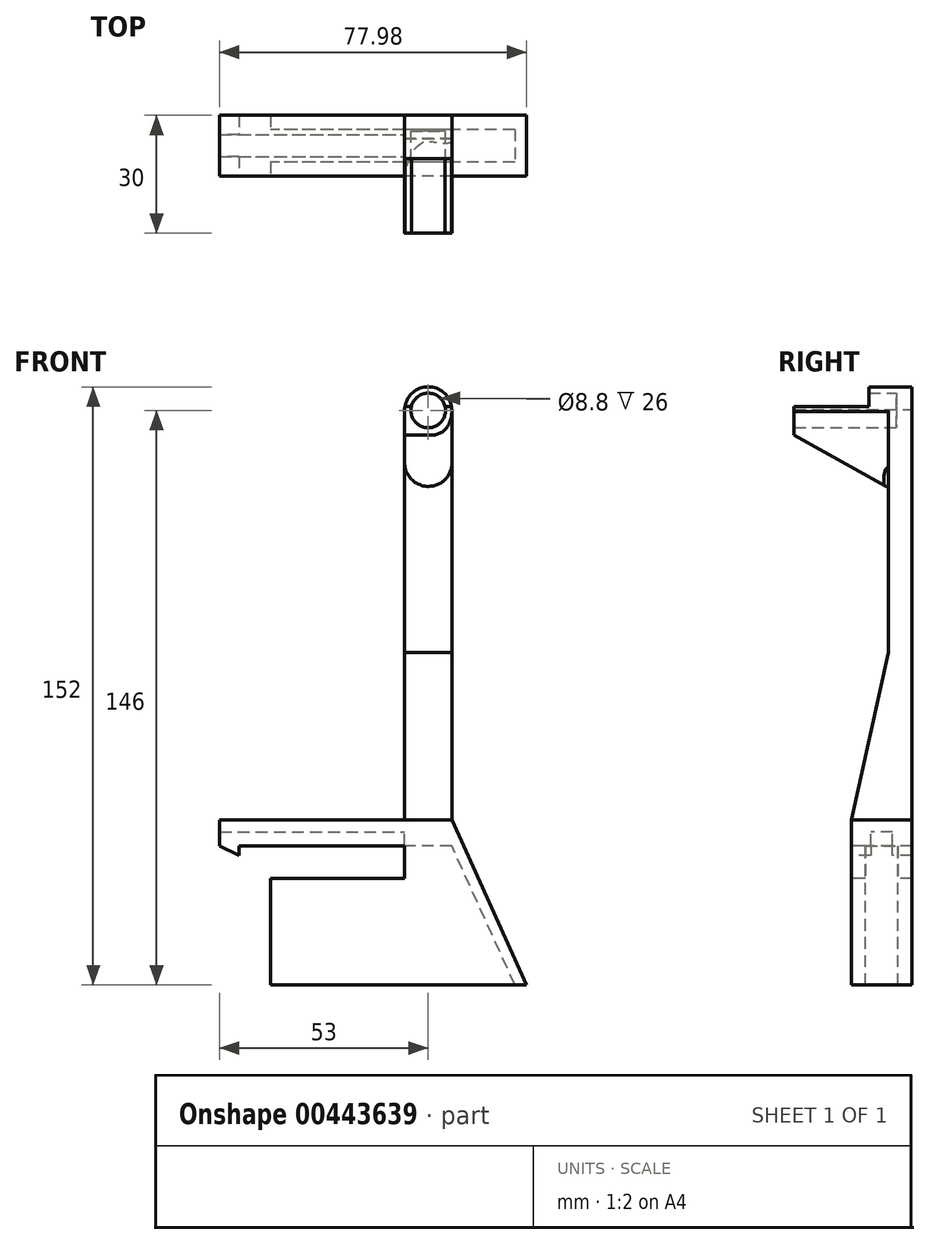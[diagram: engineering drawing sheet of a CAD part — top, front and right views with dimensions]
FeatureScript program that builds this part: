
annotation { "Feature Type Name" : "Feature", "Feature Type Description" : "" }
export const myFeature = defineFeature(function(context is Context, id is Id, definition is map)
    precondition{}
    {
        {
            var Q0;
            Q0=qCreatedBy(makeId("Front.planeOp"),FACE);
            var sketch = newSketch(context, id + "F0", { "sketchPlane" : qUnion([Q0])});
            skLineSegment(sketch, "E0.bottom", {"start": v(-6, 50) * mm, "end": v(6, 50) * mm});
            skLineSegment(sketch, "E0.top", {"start": v(-6, -50) * mm, "end": v(6, -50) * mm});
            skLineSegment(sketch, "E0.left", {"start": v(-6, 50) * mm, "end": v(-6, -50) * mm});
            skLineSegment(sketch, "E0.right", {"start": v(6, 50) * mm, "end": v(6, -50) * mm});
            skPoint(sketch, "E0.middle", {"position": v(0, 0) * mm});
            skLineSegment(sketch, "E1", {"start": v(0, 0) * mm, "end": v(0, 97.6) * mm, "construction": true});
            skCircle(sketch, "E2", {"center": v(0, 56) * mm, "radius": 6 * mm});
            skCircle(sketch, "E3", {"center": v(0, 56) * mm, "radius": 4.4 * mm});
            skLineSegment(sketch, "E4", {"start": v(-6, 56.27) * mm, "end": v(-6, 50) * mm});
            skLineSegment(sketch, "E5", {"start": v(6, 50) * mm, "end": v(6, 56) * mm});
            skSolve(sketch);
        }
        {
            var Q0;
            {var subQ0=sQuery(id+"F0.wireOp",EDGE,"E0.bottom");Q0=makeQuery(id+"F0.imprint","IMPRINT",FACE,{"disambiguationData":[TD([[makeQuery(id+"F0.imprint","IMPRINT",EDGE,{"derivedFrom":subQ0}),1.0]])]});}
            var Q1;
            Q1=makeQuery(id+"F0.imprint","IMPRINT",FACE,{"disambiguationData":[TD([[makeQuery(id+"F0.imprint","IMPRINT",EDGE,{"derivedFrom":sQuery(id+"F0.wireOp",EDGE,"E3")}),-1.0]])]});
            var Q2;
            Q2=makeQuery(id+"F0.imprint","IMPRINT",FACE,{"disambiguationData":[TD([[makeQuery(id+"F0.imprint","IMPRINT",EDGE,{"derivedFrom":sQuery(id+"F0.wireOp",EDGE,"E0.bottom")}),-1.0]])]});
            var Q3;
            Q3=makeQuery(id+"F0.imprint","IMPRINT",FACE,{"disambiguationData":[TD([[makeQuery(id+"F0.imprint","IMPRINT",EDGE,{"derivedFrom":sQuery(id+"F0.wireOp",EDGE,"E3")}),1.0]])]});
            extrude(context, id + "F1", {"entities" : qUnion([Q0, Q1, Q2, Q3]), "depth" : 6 * mm});
        }
        {
            var Q0;
            Q0=makeQuery(id+"F0.imprint","IMPRINT",FACE,{"disambiguationData":[TD([[makeQuery(id+"F0.imprint","IMPRINT",EDGE,{"derivedFrom":sQuery(id+"F0.wireOp",EDGE,"E3")}),-1.0]])]});
            extrude(context, id + "F2", {"entities" : qUnion([Q0]), "operationType" : NewBodyOperationType.ADD, "depth" : 30 * mm});
        }
        {
            var Q0;
            Q0=makeQuery(id+"F1.opExtrude","SWEPT_FACE",FACE,{"disambiguationData":[OSD([sQuery(id+"F0.wireOp",EDGE,"E0.left")])]});
            var sketch = newSketch(context, id + "F3", { "sketchPlane" : qUnion([Q0])});
            skLineSegment(sketch, "E6.bottom", {"start": v(0, -50) * mm, "end": v(15.47, -50) * mm});
            skLineSegment(sketch, "E6.top", {"start": v(0, -90) * mm, "end": v(15.47, -90) * mm});
            skLineSegment(sketch, "E6.left", {"start": v(0, -50) * mm, "end": v(0, -90) * mm});
            skLineSegment(sketch, "E6.right", {"start": v(15.47, -50) * mm, "end": v(15.47, -90) * mm});
            skPoint(sketch, "E7", {"position": v(0, -50) * mm});
            skLineSegment(sketch, "E8.bottom", {"start": v(3.61, -54.6) * mm, "end": v(11.86, -54.6) * mm});
            skLineSegment(sketch, "E8.top", {"start": v(3.61, -90) * mm, "end": v(11.86, -90) * mm});
            skLineSegment(sketch, "E8.left", {"start": v(3.61, -54.6) * mm, "end": v(3.61, -90) * mm});
            skLineSegment(sketch, "E8.right", {"start": v(11.86, -54.6) * mm, "end": v(11.86, -90) * mm});
            skPoint(sketch, "E9", {"position": v(7.74, -54.6) * mm});
            skPoint(sketch, "E10", {"position": v(7.74, -50) * mm});
            skLineSegment(sketch, "E11", {"start": v(15.47, -50) * mm, "end": v(15.47, -48) * mm});
            skLineSegment(sketch, "E12", {"start": v(15.47, -48) * mm, "end": v(6, -5.52) * mm});
            skSolve(sketch);
        }
        {
            var Q0;
            {var subQ4=sQuery(id+"F3.wireOp",EDGE,"E6.left");Q0=makeQuery(id+"F3.imprint","IMPRINT",FACE,{"disambiguationData":[TD([[makeQuery(id+"F3.imprint","IMPRINT",EDGE,{"derivedFrom":subQ4}),1.0]])]});}
            var Q1;
            {var subQ3=sQuery(id+"F3.wireOp",EDGE,"npjAtSIb-rjZG-cwZH-Mb7X-xIMRF1PIqRGn");Q1=makeQuery(id+"F3.imprint","IMPRINT",FACE,{"disambiguationData":[TD([[makeQuery(id+"F3.imprint","IMPRINT",EDGE,{"derivedFrom":subQ3}),1.0]])]});}
            var Q2;
            {var subQ3=sQuery(id+"F3.wireOp",EDGE,"E11");Q2=makeQuery(id+"F3.imprint","IMPRINT",FACE,{"disambiguationData":[TD([[makeQuery(id+"F3.imprint","IMPRINT",EDGE,{"derivedFrom":subQ3}),1.0]])]});}
            var Q3;
            Q3=makeQuery(id+"F1.opExtrude","SWEPT_FACE",FACE,{"disambiguationData":[OSD([sQuery(id+"F0.wireOp",EDGE,"E0.right"),sQuery(id+"F0.wireOp",EDGE,"E5")])]});
            extrude(context, id + "F4", {"entities" : qUnion([Q0, Q1, Q2]), "operationType" : NewBodyOperationType.ADD, "endBound" : BoundingType.UP_TO_SURFACE, "oppositeDirection" : true, "endBoundEntityFace" : qUnion([Q3]), "depth" : 25 * mm});
        }
        {
            var Q0;
            {var subQ0=sQuery(id+"F0.wireOp",EDGE,"E0.left");Q0=makeQuery(id+"F4.boolean.opBoolean","MERGE",FACE,{"derivedFrom":[makeQuery(id+"F1.opExtrude","SWEPT_FACE",FACE,{"disambiguationData":[OSD([subQ0])]}),makeQuery(id+"F4.opExtrude","CAP_FACE",FACE,{"disambiguationData":[OSD([subQ0,sQuery(id+"F3.wireOp",EDGE,"E6.bottom"),sQuery(id+"F3.wireOp",EDGE,"E6.top"),sQuery(id+"F3.wireOp",EDGE,"E6.left"),sQuery(id+"F3.wireOp",EDGE,"E6.right"),sQuery(id+"F3.wireOp",EDGE,"E8.bottom"),sQuery(id+"F3.wireOp",EDGE,"E8.left"),sQuery(id+"F3.wireOp",EDGE,"E8.right"),sQuery(id+"F3.wireOp",EDGE,"E11"),sQuery(id+"F3.wireOp",EDGE,"E12")])],"isStart":true})]});}
            var sketch = newSketch(context, id + "F5", { "sketchPlane" : qUnion([Q0])});
            skLineSegment(sketch, "E13.bottom", {"start": v(0, -48) * mm, "end": v(15.47, -48) * mm});
            skLineSegment(sketch, "E13.top", {"start": v(0, -54.6) * mm, "end": v(15.47, -54.6) * mm});
            skLineSegment(sketch, "E13.left", {"start": v(0, -48) * mm, "end": v(0, -54.6) * mm});
            skLineSegment(sketch, "E13.right", {"start": v(15.47, -48) * mm, "end": v(15.47, -54.6) * mm});
            skLineSegment(sketch, "E14.bottom", {"start": v(4.99, -54.6) * mm, "end": v(10.49, -54.6) * mm});
            skLineSegment(sketch, "E14.top", {"start": v(4.99, -51.1) * mm, "end": v(10.49, -51.1) * mm});
            skLineSegment(sketch, "E14.left", {"start": v(4.99, -54.6) * mm, "end": v(4.99, -51.1) * mm});
            skLineSegment(sketch, "E14.right", {"start": v(10.49, -54.6) * mm, "end": v(10.49, -51.1) * mm});
            skPoint(sketch, "E15", {"position": v(7.74, -51.1) * mm});
            skPoint(sketch, "E16", {"position": v(7.74, -54.6) * mm});
            skSolve(sketch);
        }
        {
            var Q0;
            Q0=makeQuery(id+"F5.imprint","IMPRINT",FACE,{"disambiguationData":[TD([[makeQuery(id+"F5.imprint","IMPRINT",EDGE,{"derivedFrom":sQuery(id+"F5.wireOp",EDGE,"E13.bottom")}),-1.0]])]});
            extrude(context, id + "F6", {"entities" : qUnion([Q0]), "operationType" : NewBodyOperationType.ADD, "depth" : 47 * mm});
        }
        {
            var Q0;
            Q0=makeQuery(id+"F6.boolean.opBoolean","MERGE",FACE,{"derivedFrom":[makeQuery(id+"F4.opExtrude","SWEPT_FACE",FACE,{"disambiguationData":[OSD([sQuery(id+"F3.wireOp",EDGE,"E6.right"),sQuery(id+"F3.wireOp",EDGE,"E11")])]}),makeQuery(id+"F6.opExtrude","SWEPT_FACE",FACE,{"disambiguationData":[OSD([sQuery(id+"F5.wireOp",EDGE,"E13.right")])]})]});
            var sketch = newSketch(context, id + "F7", { "sketchPlane" : qUnion([Q0])});
            skLineSegment(sketch, "E17", {"start": v(-53, -54.6) * mm, "end": v(-48, -54.6) * mm});
            skLineSegment(sketch, "E18", {"start": v(-48, -54.6) * mm, "end": v(-48, -57.1) * mm});
            skLineSegment(sketch, "E19", {"start": v(-48, -57.1) * mm, "end": v(-53, -54.6) * mm});
            skSolve(sketch);
        }
        {
            var Q0;
            Q0=makeQuery(id+"F7.imprint","IMPRINT",FACE,{"disambiguationData":[TD([[makeQuery(id+"F7.imprint","IMPRINT",EDGE,{"derivedFrom":sQuery(id+"F7.wireOp",EDGE,"E17")}),-1.0]])]});
            var Q1;
            Q1=makeQuery(id+"F6.opExtrude","CAP_VERTEX",VERTEX,{"disambiguationData":[OSD([sQuery(id+"F5.wireOp",EDGE,"E13.top"),sQuery(id+"F5.wireOp",EDGE,"E14.bottom"),sQuery(id+"F5.wireOp",EDGE,"E14.right")])],"isStart":false});
            extrude(context, id + "F8", {"entities" : qUnion([Q0]), "operationType" : NewBodyOperationType.ADD, "endBound" : BoundingType.UP_TO_VERTEX, "oppositeDirection" : true, "endBoundEntityVertex" : qUnion([Q1]), "depth" : 25 * mm});
        }
        {
            var Q0;
            Q0=makeQuery(id+"F7.imprint","IMPRINT",FACE,{"disambiguationData":[TD([[makeQuery(id+"F7.imprint","IMPRINT",EDGE,{"derivedFrom":sQuery(id+"F7.wireOp",EDGE,"E17")}),-1.0]])]});
            var Q1;
            Q1=makeQuery(id+"F6.opExtrude","CAP_VERTEX",VERTEX,{"disambiguationData":[OSD([sQuery(id+"F0.wireOp",EDGE,"E0.left"),sQuery(id+"F3.wireOp",EDGE,"E6.left"),sQuery(id+"F5.wireOp",EDGE,"E13.top"),sQuery(id+"F5.wireOp",EDGE,"E13.left")])],"isStart":false});
            var Q2;
            Q2=makeQuery(id+"F6.opExtrude","CAP_VERTEX",VERTEX,{"disambiguationData":[OSD([sQuery(id+"F5.wireOp",EDGE,"E13.top"),sQuery(id+"F5.wireOp",EDGE,"E14.bottom"),sQuery(id+"F5.wireOp",EDGE,"E14.left")])],"isStart":false});
            extrude(context, id + "F9", {"entities" : qUnion([Q0]), "operationType" : NewBodyOperationType.ADD, "endBound" : BoundingType.UP_TO_VERTEX, "oppositeDirection" : true, "endBoundEntityVertex" : qUnion([Q1]), "depth" : 25 * mm, "hasSecondDirection" : true, "secondDirectionBound" : SecondDirectionBoundingType.UP_TO_VERTEX, "secondDirectionOppositeDirection" : true, "secondDirectionBoundEntityVertex" : qUnion([Q2]), "secondDirectionDepth" : 25 * mm});
        }
        {
            var Q0;
            Q0=makeQuery(id+"F8.boolean.opBoolean","MERGE",FACE,{"derivedFrom":[makeQuery(id+"F6.boolean.opBoolean","MERGE",FACE,{"derivedFrom":[makeQuery(id+"F4.opExtrude","SWEPT_FACE",FACE,{"disambiguationData":[OSD([sQuery(id+"F3.wireOp",EDGE,"E6.right"),sQuery(id+"F3.wireOp",EDGE,"E11")])]}),makeQuery(id+"F6.opExtrude","SWEPT_FACE",FACE,{"disambiguationData":[OSD([sQuery(id+"F5.wireOp",EDGE,"E13.right")])]})]}),makeQuery(id+"F8.opExtrude","CAP_FACE",FACE,{"disambiguationData":[OSD([sQuery(id+"F7.wireOp",EDGE,"E17"),sQuery(id+"F7.wireOp",EDGE,"E18"),sQuery(id+"F7.wireOp",EDGE,"E19")])],"isStart":true})]});
            var sketch = newSketch(context, id + "F10", { "sketchPlane" : qUnion([Q0])});
            skLineSegment(sketch, "E20.bottom", {"start": v(-6, -90) * mm, "end": v(-40, -90) * mm});
            skLineSegment(sketch, "E20.top", {"start": v(-6, -62.85) * mm, "end": v(-40, -62.85) * mm});
            skLineSegment(sketch, "E20.left", {"start": v(-6, -90) * mm, "end": v(-6, -62.85) * mm});
            skLineSegment(sketch, "E20.right", {"start": v(-40, -90) * mm, "end": v(-40, -62.85) * mm});
            skSolve(sketch);
        }
        {
            var Q0;
            Q0=makeQuery(id+"F10.imprint","IMPRINT",FACE,{"disambiguationData":[TD([[makeQuery(id+"F10.imprint","IMPRINT",EDGE,{"derivedFrom":sQuery(id+"F10.wireOp",EDGE,"E20.bottom")}),-1.0]])]});
            var Q1;
            Q1=makeQuery(id+"F4.opExtrude","SWEPT_FACE",FACE,{"disambiguationData":[OSD([sQuery(id+"F3.wireOp",EDGE,"E8.right")])]});
            extrude(context, id + "F11", {"entities" : qUnion([Q0]), "operationType" : NewBodyOperationType.ADD, "endBound" : BoundingType.UP_TO_SURFACE, "oppositeDirection" : true, "endBoundEntityFace" : qUnion([Q1]), "depth" : 25 * mm});
        }
        {
            var Q0;
            Q0=makeQuery(id+"F10.imprint","IMPRINT",FACE,{"disambiguationData":[TD([[makeQuery(id+"F10.imprint","IMPRINT",EDGE,{"derivedFrom":sQuery(id+"F10.wireOp",EDGE,"E20.bottom")}),-1.0]])]});
            var Q1;
            Q1=makeQuery(id+"F9.boolean.opBoolean","MERGE",FACE,{"derivedFrom":[makeQuery(id+"F6.boolean.opBoolean","MERGE",FACE,{"derivedFrom":[makeQuery(id+"F4.boolean.opBoolean","MERGE",FACE,{"derivedFrom":[makeQuery(id+"F1.opExtrude","CAP_FACE",FACE,{"disambiguationData":[OSD([sQuery(id+"F0.wireOp",EDGE,"E0.top"),sQuery(id+"F0.wireOp",EDGE,"E0.left"),sQuery(id+"F0.wireOp",EDGE,"E0.right"),sQuery(id+"F0.wireOp",EDGE,"E2"),sQuery(id+"F0.wireOp",EDGE,"E4"),sQuery(id+"F0.wireOp",EDGE,"E5")])],"isStart":true}),makeQuery(id+"F4.opExtrude","SWEPT_FACE",FACE,{"disambiguationData":[OSD([sQuery(id+"F3.wireOp",EDGE,"E6.left")])]})]}),makeQuery(id+"F6.opExtrude","SWEPT_FACE",FACE,{"disambiguationData":[OSD([sQuery(id+"F5.wireOp",EDGE,"E13.left")])]})]}),makeQuery(id+"F9.opExtrude","CAP_FACE",FACE,{"disambiguationData":[OSD([dummyQuery(id+"F9.vertexPlane.planeOp",FACE)])],"isStart":false})]});
            var Q2;
            Q2=makeQuery(id+"F4.opExtrude","SWEPT_FACE",FACE,{"disambiguationData":[OSD([sQuery(id+"F3.wireOp",EDGE,"E8.left")])]});
            extrude(context, id + "F12", {"entities" : qUnion([Q0]), "operationType" : NewBodyOperationType.ADD, "endBound" : BoundingType.UP_TO_SURFACE, "oppositeDirection" : true, "endBoundEntityFace" : qUnion([Q1]), "depth" : 25 * mm, "hasSecondDirection" : true, "secondDirectionBound" : SecondDirectionBoundingType.UP_TO_SURFACE, "secondDirectionOppositeDirection" : true, "secondDirectionBoundEntityFace" : qUnion([Q2]), "secondDirectionDepth" : 25 * mm});
        }
        {
            var Q0;
            Q0=makeQuery(id+"F11.boolean.opBoolean","MERGE",FACE,{"derivedFrom":[makeQuery(id+"F8.boolean.opBoolean","MERGE",FACE,{"derivedFrom":[makeQuery(id+"F6.boolean.opBoolean","MERGE",FACE,{"derivedFrom":[makeQuery(id+"F4.opExtrude","SWEPT_FACE",FACE,{"disambiguationData":[OSD([sQuery(id+"F3.wireOp",EDGE,"E6.right"),sQuery(id+"F3.wireOp",EDGE,"E11")])]}),makeQuery(id+"F6.opExtrude","SWEPT_FACE",FACE,{"disambiguationData":[OSD([sQuery(id+"F5.wireOp",EDGE,"E13.right")])]})]}),makeQuery(id+"F8.opExtrude","CAP_FACE",FACE,{"disambiguationData":[OSD([sQuery(id+"F7.wireOp",EDGE,"E17"),sQuery(id+"F7.wireOp",EDGE,"E18"),sQuery(id+"F7.wireOp",EDGE,"E19")])],"isStart":true})]}),makeQuery(id+"F11.opExtrude","CAP_FACE",FACE,{"disambiguationData":[OSD([sQuery(id+"F10.wireOp",EDGE,"E20.bottom"),sQuery(id+"F10.wireOp",EDGE,"E20.top"),sQuery(id+"F10.wireOp",EDGE,"E20.left"),sQuery(id+"F10.wireOp",EDGE,"E20.right")])],"isStart":true})]});
            var sketch = newSketch(context, id + "F13", { "sketchPlane" : qUnion([Q0])});
            skLineSegment(sketch, "E21", {"start": v(6, -90) * mm, "end": v(22, -90) * mm});
            skLineSegment(sketch, "E22", {"start": v(22, -90) * mm, "end": v(6, -54.6) * mm});
            skLineSegment(sketch, "E23", {"start": v(6, -54.6) * mm, "end": v(6, -90) * mm});
            skPoint(sketch, "E24.0", {"position": v(6, -54.6) * mm});
            skSolve(sketch);
        }
        {
            var Q0;
            Q0=makeQuery(id+"F13.imprint","IMPRINT",FACE,{"disambiguationData":[TD([[makeQuery(id+"F13.imprint","IMPRINT",EDGE,{"derivedFrom":sQuery(id+"F13.wireOp",EDGE,"E21")}),1.0]])]});
            var Q1;
            {var subQ0=sQuery(id+"F3.wireOp",EDGE,"E8.right");Q1=makeQuery(id+"F11.boolean.opBoolean","MERGE",FACE,{"derivedFrom":[makeQuery(id+"F4.opExtrude","SWEPT_FACE",FACE,{"disambiguationData":[OSD([subQ0])]}),makeQuery(id+"F11.opExtrude","CAP_FACE",FACE,{"disambiguationData":[OSD([subQ0])],"isStart":false})]});}
            extrude(context, id + "F14", {"entities" : qUnion([Q0]), "operationType" : NewBodyOperationType.ADD, "endBound" : BoundingType.UP_TO_SURFACE, "oppositeDirection" : true, "endBoundEntityFace" : qUnion([Q1]), "depth" : 25 * mm});
        }
        {
            var Q0;
            Q0=makeQuery(id+"F14.boolean.opBoolean","MERGE",FACE,{"derivedFrom":[makeQuery(id+"F11.boolean.opBoolean","MERGE",FACE,{"derivedFrom":[makeQuery(id+"F8.boolean.opBoolean","MERGE",FACE,{"derivedFrom":[makeQuery(id+"F6.boolean.opBoolean","MERGE",FACE,{"derivedFrom":[makeQuery(id+"F4.opExtrude","SWEPT_FACE",FACE,{"disambiguationData":[OSD([sQuery(id+"F3.wireOp",EDGE,"E6.right"),sQuery(id+"F3.wireOp",EDGE,"E11")])]}),makeQuery(id+"F6.opExtrude","SWEPT_FACE",FACE,{"disambiguationData":[OSD([sQuery(id+"F5.wireOp",EDGE,"E13.right")])]})]}),makeQuery(id+"F8.opExtrude","CAP_FACE",FACE,{"disambiguationData":[OSD([sQuery(id+"F7.wireOp",EDGE,"E17"),sQuery(id+"F7.wireOp",EDGE,"E18"),sQuery(id+"F7.wireOp",EDGE,"E19")])],"isStart":true})]}),makeQuery(id+"F11.opExtrude","CAP_FACE",FACE,{"disambiguationData":[OSD([sQuery(id+"F10.wireOp",EDGE,"E20.bottom"),sQuery(id+"F10.wireOp",EDGE,"E20.top"),sQuery(id+"F10.wireOp",EDGE,"E20.left"),sQuery(id+"F10.wireOp",EDGE,"E20.right")])],"isStart":true})]}),makeQuery(id+"F14.opExtrude","CAP_FACE",FACE,{"disambiguationData":[OSD([sQuery(id+"F13.wireOp",EDGE,"E21"),sQuery(id+"F13.wireOp",EDGE,"E22"),sQuery(id+"F13.wireOp",EDGE,"E23")])],"isStart":true})]});
            var sketch = newSketch(context, id + "F15", { "sketchPlane" : qUnion([Q0])});
            skLineSegment(sketch, "E25", {"start": v(6, -48) * mm, "end": v(24.98, -90) * mm});
            skLineSegment(sketch, "E26.0", {"start": v(22, -90) * mm, "end": v(6, -54.6) * mm});
            skLineSegment(sketch, "E27", {"start": v(22, -90) * mm, "end": v(24.98, -90) * mm});
            skSolve(sketch);
        }
        {
            var Q0;
            Q0=makeQuery(id+"F15.imprint","IMPRINT",FACE,{"disambiguationData":[TD([[makeQuery(id+"F15.imprint","IMPRINT",EDGE,{"derivedFrom":sQuery(id+"F15.wireOp",EDGE,"E25")}),-1.0]])]});
            var Q1;
            {var subQ0=dummyQuery(id+"F9.vertexPlane.planeOp",FACE);var subQ1=sQuery(id+"F5.wireOp",EDGE,"E13.left");var subQ2=sQuery(id+"F3.wireOp",EDGE,"E6.left");var subQ3=sQuery(id+"F0.wireOp",EDGE,"E5");var subQ4=sQuery(id+"F0.wireOp",EDGE,"E4");var subQ5=sQuery(id+"F0.wireOp",EDGE,"E2");var subQ6=sQuery(id+"F0.wireOp",EDGE,"E0.right");var subQ7=sQuery(id+"F0.wireOp",EDGE,"E0.left");var subQ8=sQuery(id+"F0.wireOp",EDGE,"E0.top");Q1=makeQuery(id+"F12.boolean.opBoolean","MERGE",FACE,{"derivedFrom":[makeQuery(id+"F9.boolean.opBoolean","MERGE",FACE,{"derivedFrom":[makeQuery(id+"F6.boolean.opBoolean","MERGE",FACE,{"derivedFrom":[makeQuery(id+"F4.boolean.opBoolean","MERGE",FACE,{"derivedFrom":[makeQuery(id+"F1.opExtrude","CAP_FACE",FACE,{"disambiguationData":[OSD([subQ8,subQ7,subQ6,subQ5,subQ4,subQ3])],"isStart":true}),makeQuery(id+"F4.opExtrude","SWEPT_FACE",FACE,{"disambiguationData":[OSD([subQ2])]})]}),makeQuery(id+"F6.opExtrude","SWEPT_FACE",FACE,{"disambiguationData":[OSD([subQ1])]})]}),makeQuery(id+"F9.opExtrude","CAP_FACE",FACE,{"disambiguationData":[OSD([subQ0])],"isStart":false})]}),makeQuery(id+"F12.opExtrude","CAP_FACE",FACE,{"disambiguationData":[OSD([subQ8,subQ7,subQ6,subQ5,subQ4,subQ3,subQ2,subQ1,subQ0])],"isStart":false})]});}
            extrude(context, id + "F16", {"entities" : qUnion([Q0]), "operationType" : NewBodyOperationType.ADD, "endBound" : BoundingType.UP_TO_SURFACE, "oppositeDirection" : true, "endBoundEntityFace" : qUnion([Q1]), "depth" : 25 * mm});
        }
        {
            var Q0;
            {var subQ0=dummyQuery(id+"F9.vertexPlane.planeOp",FACE);var subQ1=sQuery(id+"F5.wireOp",EDGE,"E13.left");var subQ2=sQuery(id+"F3.wireOp",EDGE,"E6.left");var subQ3=sQuery(id+"F0.wireOp",EDGE,"E5");var subQ4=sQuery(id+"F0.wireOp",EDGE,"E4");var subQ5=sQuery(id+"F0.wireOp",EDGE,"E2");var subQ6=sQuery(id+"F0.wireOp",EDGE,"E0.right");var subQ7=sQuery(id+"F0.wireOp",EDGE,"E0.left");var subQ8=sQuery(id+"F0.wireOp",EDGE,"E0.top");Q0=makeQuery(id+"F16.boolean.opBoolean","MERGE",FACE,{"derivedFrom":[makeQuery(id+"F12.boolean.opBoolean","MERGE",FACE,{"derivedFrom":[makeQuery(id+"F9.boolean.opBoolean","MERGE",FACE,{"derivedFrom":[makeQuery(id+"F6.boolean.opBoolean","MERGE",FACE,{"derivedFrom":[makeQuery(id+"F4.boolean.opBoolean","MERGE",FACE,{"derivedFrom":[makeQuery(id+"F1.opExtrude","CAP_FACE",FACE,{"disambiguationData":[OSD([subQ8,subQ7,subQ6,subQ5,subQ4,subQ3])],"isStart":true}),makeQuery(id+"F4.opExtrude","SWEPT_FACE",FACE,{"disambiguationData":[OSD([subQ2])]})]}),makeQuery(id+"F6.opExtrude","SWEPT_FACE",FACE,{"disambiguationData":[OSD([subQ1])]})]}),makeQuery(id+"F9.opExtrude","CAP_FACE",FACE,{"disambiguationData":[OSD([subQ0])],"isStart":false})]}),makeQuery(id+"F12.opExtrude","CAP_FACE",FACE,{"disambiguationData":[OSD([subQ8,subQ7,subQ6,subQ5,subQ4,subQ3,subQ2,subQ1,subQ0])],"isStart":false})]}),makeQuery(id+"F16.opExtrude","CAP_FACE",FACE,{"disambiguationData":[OSD([subQ8,subQ7,subQ6,subQ5,subQ4,subQ3,subQ2,subQ1,subQ0])],"isStart":false})]});}
            var sketch = newSketch(context, id + "F17", { "sketchPlane" : qUnion([Q0])});
            skLineSegment(sketch, "E28", {"start": v(-22, -90) * mm, "end": v(-6, -90) * mm});
            skLineSegment(sketch, "E29", {"start": v(-6, -90) * mm, "end": v(-6, -54.6) * mm});
            skLineSegment(sketch, "E30", {"start": v(-6, -54.6) * mm, "end": v(-22, -90) * mm});
            skSolve(sketch);
        }
        {
            var Q0;
            Q0 = qSketchRegion(id + "F17", true);
            var Q1;
            {var subQ0=sQuery(id+"F3.wireOp",EDGE,"E8.left");Q1=makeQuery(id+"F12.boolean.opBoolean","MERGE",FACE,{"derivedFrom":[makeQuery(id+"F4.opExtrude","SWEPT_FACE",FACE,{"disambiguationData":[OSD([subQ0])]}),makeQuery(id+"F12.opExtrude","CAP_FACE",FACE,{"disambiguationData":[OSD([subQ0])],"isStart":true})]});}
            extrude(context, id + "F18", {"entities" : qUnion([Q0]), "operationType" : NewBodyOperationType.ADD, "endBound" : BoundingType.UP_TO_SURFACE, "oppositeDirection" : true, "endBoundEntityFace" : qUnion([Q1]), "depth" : 25 * mm});
        }
        {
            var Q0;
            Q0=makeQuery(id+"F2.opExtrude","CAP_FACE",FACE,{"disambiguationData":[OSD([sQuery(id+"F0.wireOp",EDGE,"E2"),sQuery(id+"F0.wireOp",EDGE,"E3"),sQuery(id+"F0.wireOp",EDGE,"E4")])],"isStart":false});
            var sketch = newSketch(context, id + "F19", { "sketchPlane" : qUnion([Q0])});
            skLineSegment(sketch, "E31", {"start": v(0, 56) * mm, "end": v(-9.13, 56) * mm, "construction": true});
            skLineSegment(sketch, "E32", {"start": v(-9.13, 56) * mm, "end": v(8.88, 56) * mm, "construction": true});
            skPoint(sketch, "E32.endSnap0", {"position": v(-4.57, 56) * mm});
            skLineSegment(sketch, "E33", {"start": v(-10.48, 57) * mm, "end": v(15.02, 57) * mm});
            skSolve(sketch);
        }
        {
            var Q0;
            {var subQ0=sQuery(id+"F19.wireOp",EDGE,"E33");var subQ1=makeQuery(id+"F2.opExtrude","CAP_EDGE",EDGE,{"disambiguationData":[OSD([sQuery(id+"F0.wireOp",EDGE,"E2")])],"isStart":false});var subQ2=makeQuery(id+"F19.imprint","INTERSECT",VERTEX,{"disambiguationData":[OD(0.0)],"derivedFrom":[subQ1,subQ0]});Q0=makeQuery(id+"F19.imprint","IMPRINT",FACE,{"disambiguationData":[TD([[makeQuery(id+"F19.imprint","IMPRINT",EDGE,{"disambiguationData":[TD([[subQ2,-1.0]])],"derivedFrom":subQ0}),1.0]])]});}
            extrude(context, id + "F20", {"entities" : qUnion([Q0]), "operationType" : NewBodyOperationType.REMOVE, "oppositeDirection" : true, "depth" : 21 * mm});
        }
        {
            var Q0;
            Q0=makeQuery(id+"F2.opExtrude","CAP_FACE",FACE,{"disambiguationData":[OSD([sQuery(id+"F0.wireOp",EDGE,"E2"),sQuery(id+"F0.wireOp",EDGE,"E3"),sQuery(id+"F0.wireOp",EDGE,"E4")])],"isStart":false});
            var sketch = newSketch(context, id + "F21", { "sketchPlane" : qUnion([Q0])});
            skPoint(sketch, "E34", {"position": v(-6, 55.74) * mm});
            skPoint(sketch, "E35", {"position": v(6, 55.74) * mm});
            skLineSegment(sketch, "E36", {"start": v(-6, 55.74) * mm, "end": v(-6, 42.74) * mm});
            skLineSegment(sketch, "E37", {"start": v(6, 55.74) * mm, "end": v(6, 41.74) * mm});
            skArc(sketch, "E38", {"start": v(-6, 42.74) * mm, "mid": v(-0.46, 36.72) * mm, "end": v(6, 41.74) * mm});
            skSolve(sketch);
        }
        {
            var Q0;
            {var subQ0=sQuery(id+"F21.wireOp",EDGE,"E36");Q0=makeQuery(id+"F21.imprint","IMPRINT",FACE,{"disambiguationData":[TD([[makeQuery(id+"F21.imprint","IMPRINT",EDGE,{"derivedFrom":subQ0}),1.0]])]});}
            var Q1;
            {var subQ0=sQuery(id+"F0.wireOp",EDGE,"E5");var subQ1=sQuery(id+"F0.wireOp",EDGE,"E0.right");var subQ2=sQuery(id+"F0.wireOp",EDGE,"E2");var subQ3=sQuery(id+"F0.wireOp",EDGE,"E0.left");var subQ4=sQuery(id+"F0.wireOp",EDGE,"E0.top");var subQ5=sQuery(id+"F0.wireOp",EDGE,"E4");Q1=makeQuery(id+"F2.boolean.opBoolean","SPLIT",FACE,{"disambiguationData":[TD([makeQuery(id+"F1.opExtrude","SWEPT_FACE",FACE,{"disambiguationData":[OSD([subQ4])]})])],"derivedFrom":makeQuery(id+"F1.opExtrude","CAP_FACE",FACE,{"disambiguationData":[OSD([subQ4,subQ3,subQ1,subQ2,subQ5,subQ0])],"isStart":false})});}
            extrude(context, id + "F22", {"entities" : qUnion([Q0]), "operationType" : NewBodyOperationType.ADD, "endBound" : BoundingType.UP_TO_SURFACE, "oppositeDirection" : true, "endBoundEntityFace" : qUnion([Q1]), "depth" : 25 * mm});
        }
        {
            var Q0;
            Q0=makeQuery(id+"F2.boolean.opBoolean","SPLIT",FACE,{"disambiguationData":[TD([makeQuery(id+"F2.opExtrude","SWEPT_FACE",FACE,{"disambiguationData":[OSD([sQuery(id+"F0.wireOp",EDGE,"E3")])]})])],"derivedFrom":makeQuery(id+"F1.opExtrude","CAP_FACE",FACE,{"disambiguationData":[OSD([sQuery(id+"F0.wireOp",EDGE,"E0.top"),sQuery(id+"F0.wireOp",EDGE,"E0.left"),sQuery(id+"F0.wireOp",EDGE,"E0.right"),sQuery(id+"F0.wireOp",EDGE,"E2"),sQuery(id+"F0.wireOp",EDGE,"E4"),sQuery(id+"F0.wireOp",EDGE,"E5")])],"isStart":false})});
            extrude(context, id + "F23", {"entities" : qUnion([Q0]), "operationType" : NewBodyOperationType.REMOVE, "oppositeDirection" : true, "depth" : 2 * mm});
        }
        {
            var Q0;
            Q0=makeQuery(id+"F23.boolean.opBoolean","COPY",FACE,{"derivedFrom":makeQuery(id+"F23.opExtrude","CAP_FACE",FACE,{"disambiguationData":[OSD([sQuery(id+"F0.wireOp",EDGE,"E0.top"),sQuery(id+"F0.wireOp",EDGE,"E0.left"),sQuery(id+"F0.wireOp",EDGE,"E0.right"),sQuery(id+"F0.wireOp",EDGE,"E2"),sQuery(id+"F0.wireOp",EDGE,"E4"),sQuery(id+"F0.wireOp",EDGE,"E5")])],"isStart":false})});
            extrude(context, id + "F24", {"entities" : qUnion([Q0]), "operationType" : NewBodyOperationType.ADD, "oppositeDirection" : true, "depth" : 2 * mm});
        }
        {
            var Q0;
            Q0=makeQuery(id+"F20.boolean.opBoolean","COPY",FACE,{"derivedFrom":makeQuery(id+"F20.opExtrude","CAP_FACE",FACE,{"disambiguationData":[OSD([sQuery(id+"F0.wireOp",EDGE,"E2"),sQuery(id+"F0.wireOp",EDGE,"E3"),sQuery(id+"F19.wireOp",EDGE,"E33")])],"isStart":false})});
            extrude(context, id + "F25", {"entities" : qUnion([Q0]), "operationType" : NewBodyOperationType.ADD, "depth" : 2 * mm});
        }
        {
            var Q0;
            Q0=makeQuery(id+"F22.opExtrude","SWEPT_FACE",FACE,{"disambiguationData":[OSD([sQuery(id+"F21.wireOp",EDGE,"E36")])]});
            var sketch = newSketch(context, id + "F26", { "sketchPlane" : qUnion([Q0])});
            skLineSegment(sketch, "E39.bottom", {"start": v(6, 55.74) * mm, "end": v(30, 55.74) * mm});
            skLineSegment(sketch, "E39.top", {"start": v(6, 36.36) * mm, "end": v(30, 36.36) * mm});
            skLineSegment(sketch, "E39.left", {"start": v(6, 55.74) * mm, "end": v(6, 36.36) * mm});
            skLineSegment(sketch, "E39.right", {"start": v(30, 55.74) * mm, "end": v(30, 36.36) * mm});
            skLineSegment(sketch, "E40", {"start": v(6, 36.36) * mm, "end": v(30, 49.74) * mm});
            skSolve(sketch);
        }
        {
            var Q0;
            {var subQ0=sQuery(id+"F26.wireOp",EDGE,"E39.top");Q0=makeQuery(id+"F26.imprint","IMPRINT",FACE,{"disambiguationData":[TD([[makeQuery(id+"F26.imprint","IMPRINT",EDGE,{"derivedFrom":subQ0}),1.0]])]});}
            var Q1;
            {var subQ0=sQuery(id+"F26.wireOp",EDGE,"E39.right");var subQ3=sQuery(id+"F26.wireOp",EDGE,"E40");var subQ4=makeQuery(id+"F26.imprint","INTERSECT",VERTEX,{"derivedFrom":[subQ0,subQ3]});Q1=makeQuery(id+"F26.imprint","IMPRINT",FACE,{"disambiguationData":[TD([[makeQuery(id+"F26.imprint","IMPRINT",EDGE,{"disambiguationData":[TD([[subQ4,-1.0]])],"derivedFrom":subQ0}),-1.0]])]});}
            extrude(context, id + "F27", {"entities" : qUnion([Q0, Q1]), "operationType" : NewBodyOperationType.REMOVE, "oppositeDirection" : true, "depth" : 25 * mm});
        }
        {
            var Q0;
            Q0=makeQuery(id+"F27.boolean.opBoolean","COPY",EDGE,{"derivedFrom":makeQuery(id+"F27.opExtrude","CAP_EDGE",EDGE,{"disambiguationData":[OSD([sQuery(id+"F26.wireOp",EDGE,"E40")])],"isStart":true})});
            var Q1;
            Q1=makeQuery(id+"F27.boolean.opBoolean","INTERSECT",EDGE,{"derivedFrom":[makeQuery(id+"F22.opExtrude","SWEPT_FACE",FACE,{"disambiguationData":[OSD([sQuery(id+"F21.wireOp",EDGE,"E37")])]}),makeQuery(id+"F27.opExtrude","SWEPT_FACE",FACE,{"disambiguationData":[OSD([sQuery(id+"F26.wireOp",EDGE,"E40")])]})]});
            fillet(context, id + "F28", {"entities" : qUnion([Q0, Q1]), "radius" : 5 * mm, "tangentPropagation" : true, "allowEdgeOverflow" : false});
        }
    });
